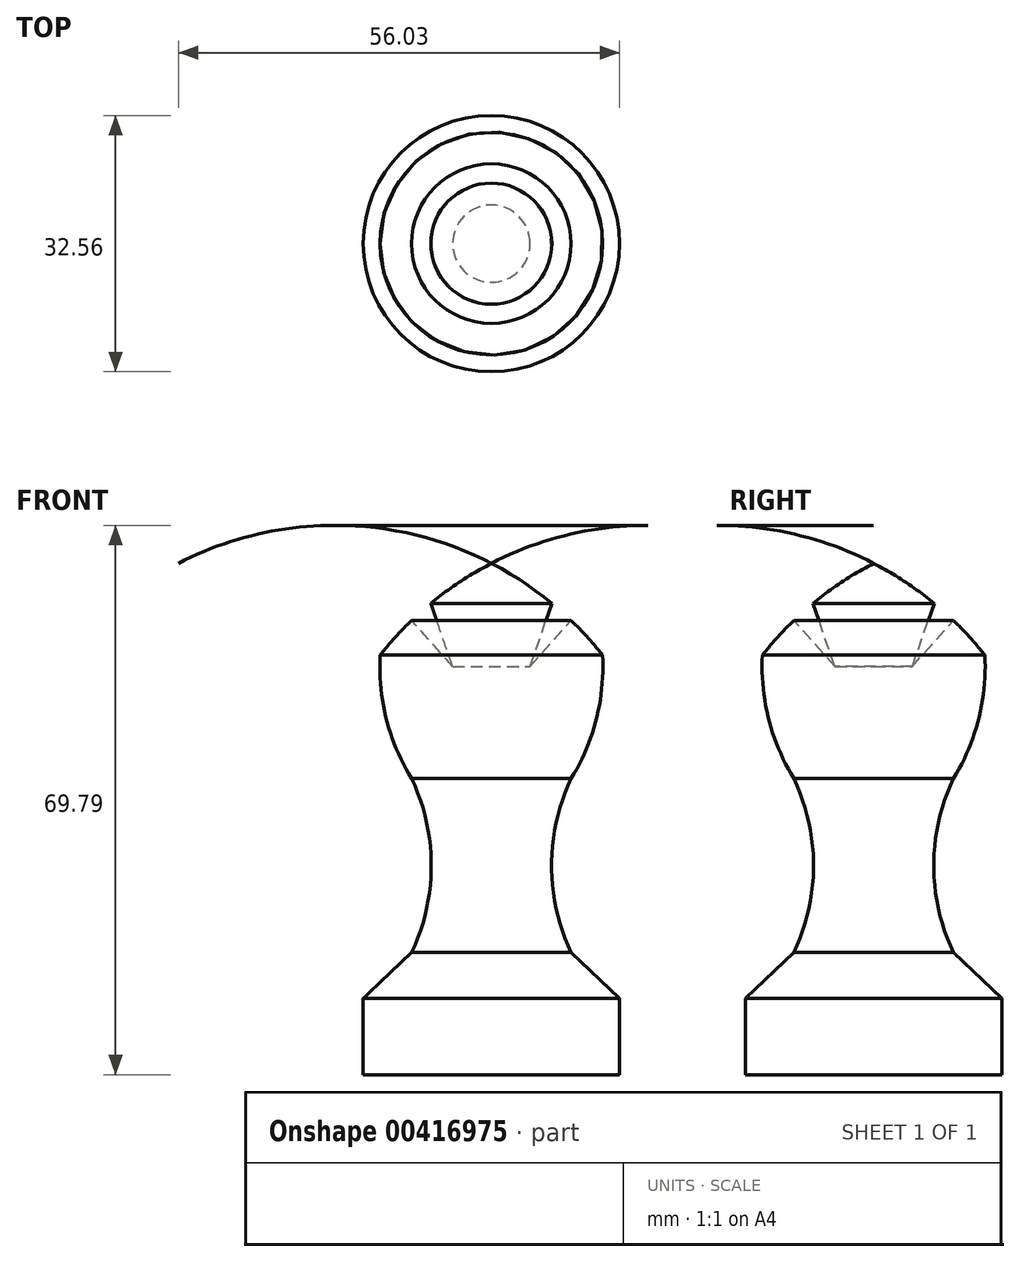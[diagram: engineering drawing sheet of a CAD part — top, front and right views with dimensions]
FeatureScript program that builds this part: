
annotation { "Feature Type Name" : "Feature", "Feature Type Description" : "" }
export const myFeature = defineFeature(function(context is Context, id is Id, definition is map)
    precondition{}
    {
        {
            var Q0;
            Q0=qCreatedBy(makeId("Front.planeOp"),FACE);
            var sketch = newSketch(context, id + "F0", { "sketchPlane" : qUnion([Q0])});
            skArc(sketch, "E0", {"start": v(14.13, 53.29) * mm, "mid": v(7.69, 59.88) * mm, "end": v(0, 64.96) * mm});
            skArc(sketch, "E1", {"start": v(10.14, 37.62) * mm, "mid": v(13.33, 45.15) * mm, "end": v(14.13, 53.29) * mm});
            skArc(sketch, "E2", {"start": v(10.14, 37.62) * mm, "mid": v(7.63, 26.57) * mm, "end": v(10.14, 15.51) * mm});
            skLineSegment(sketch, "E3", {"start": v(10.14, 15.51) * mm, "end": v(16.28, 9.67) * mm});
            skLineSegment(sketch, "E4", {"start": v(16.28, 9.67) * mm, "end": v(16.28, 0) * mm});
            skLineSegment(sketch, "E5", {"start": v(16.28, 0) * mm, "end": v(0, 0) * mm});
            skLineSegment(sketch, "E6", {"start": v(0, 0) * mm, "end": v(0, 64.96) * mm});
            skLineSegment(sketch, "E7", {"start": v(7.69, 59.88) * mm, "end": v(4.91, 51.85) * mm});
            skLineSegment(sketch, "E8", {"start": v(4.91, 51.85) * mm, "end": v(10.14, 57.7) * mm});
            skSolve(sketch);
        }
        {
            var Q0;
            {var subQ0=sQuery(id+"F0.wireOp",EDGE,"E1");Q0=makeQuery(id+"F0.imprint","IMPRINT",FACE,{"disambiguationData":[TD([[makeQuery(id+"F0.imprint","IMPRINT",EDGE,{"derivedFrom":subQ0}),1.0]])]});}
            var Q1;
            Q1=sQuery(id+"F0.wireOp",EDGE,"E6");
            revolve(context, id + "F1", {"entities" : qUnion([Q0]), "axis" : qUnion([Q1]), "revolveType" : RevolveType.FULL});
        }
    });
